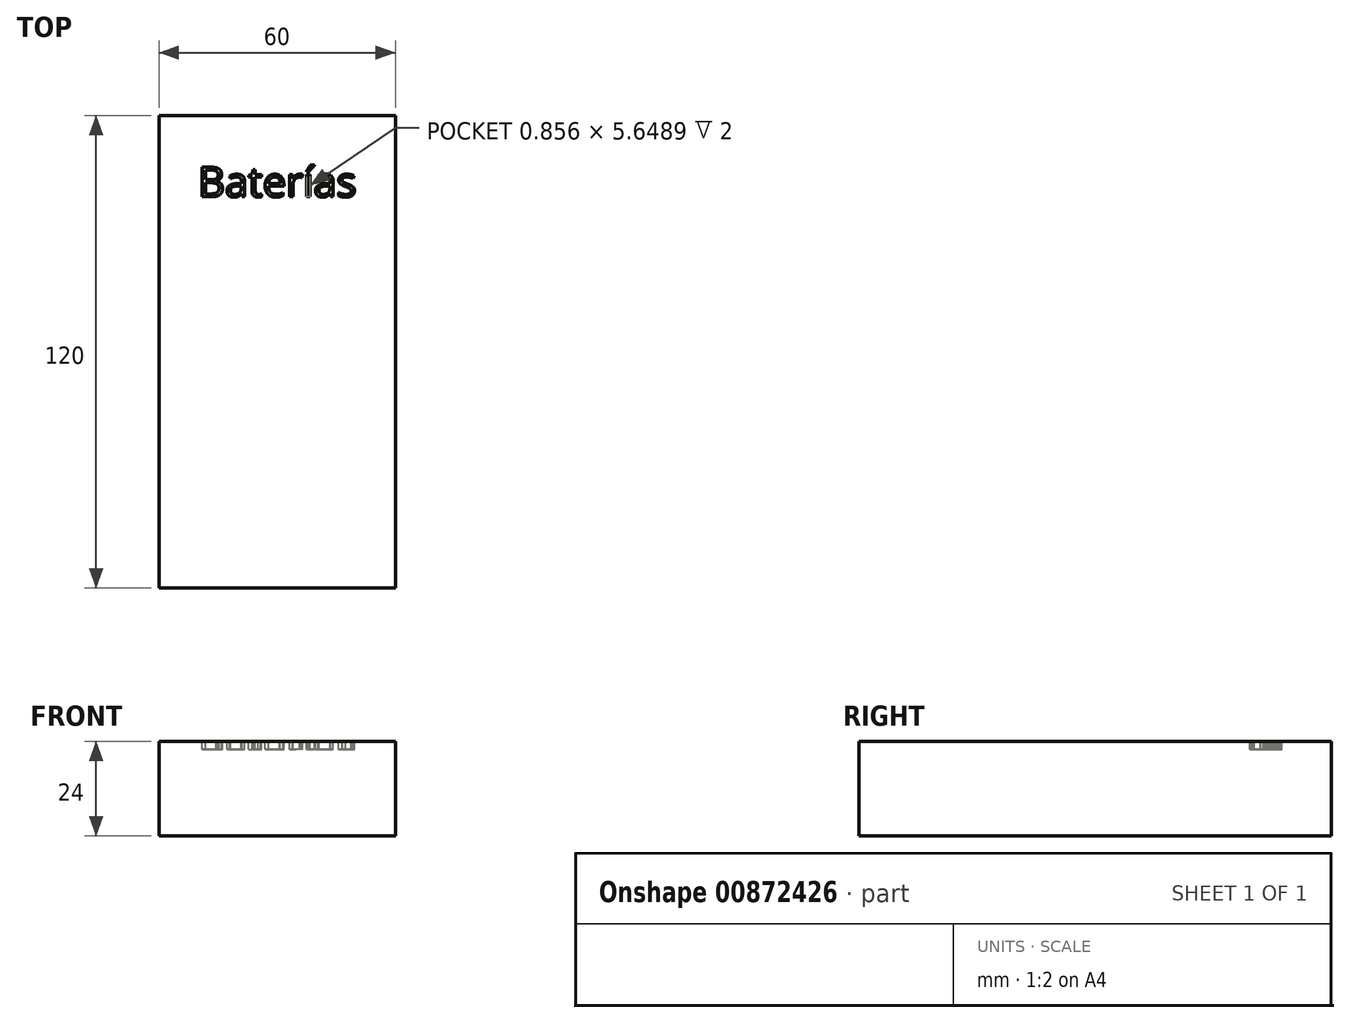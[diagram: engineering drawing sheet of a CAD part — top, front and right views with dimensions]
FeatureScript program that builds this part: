
annotation { "Feature Type Name" : "Feature", "Feature Type Description" : "" }
export const myFeature = defineFeature(function(context is Context, id is Id, definition is map)
    precondition{}
    {
        {
            var Q0;
            Q0=qCreatedBy(makeId("Top.planeOp"),FACE);
            var sketch = newSketch(context, id + "F0", { "sketchPlane" : qUnion([Q0])});
            skLineSegment(sketch, "E0.bottom", {"start": v(30, -60) * mm, "end": v(-30, -60) * mm});
            skLineSegment(sketch, "E0.top", {"start": v(30, 60) * mm, "end": v(-30, 60) * mm});
            skLineSegment(sketch, "E0.left", {"start": v(30, -60) * mm, "end": v(30, 60) * mm});
            skLineSegment(sketch, "E0.right", {"start": v(-30, -60) * mm, "end": v(-30, 60) * mm});
            skPoint(sketch, "E0.middle", {"position": v(0, 0) * mm});
            skSolve(sketch);
        }
        {
            var Q0;
            Q0=makeQuery(id+"F0.imprint","IMPRINT",FACE,{"disambiguationData":[TD([[makeQuery(id+"F0.imprint","IMPRINT",EDGE,{"derivedFrom":sQuery(id+"F0.wireOp",EDGE,"E0.bottom")}),-1.0]])]});
            extrude(context, id + "F1", {"entities" : qUnion([Q0]), "depth" : 24 * mm, "offsetDistance" : 25 * mm});
        }
        {
            var Q0;
            Q0=makeQuery(id+"F1.opExtrude","CAP_FACE",FACE,{"disambiguationData":[OSD([sQuery(id+"F0.wireOp",EDGE,"E0.bottom"),sQuery(id+"F0.wireOp",EDGE,"E0.top"),sQuery(id+"F0.wireOp",EDGE,"E0.left"),sQuery(id+"F0.wireOp",EDGE,"E0.right")])],"isStart":false});
            var sketch = newSketch(context, id + "F2", { "sketchPlane" : qUnion([Q0])});
            skText(sketch, "E1", { "text": "Baterías", "fontName": "OpenSans-Regular.ttf"});
            const initialGuessF2  = {"E1": [-0.02013, 0.03938, 1, 0, 0.0076]};
            skSetInitialGuess(sketch, initialGuessF2);
            skSolve(sketch);
        }
        {
            var Q0;
            Q0=makeQuery(id+"F2.imprint","IMPRINT",FACE,{"disambiguationData":[TD([[makeQuery(id+"F2.imprint","IMPRINT",EDGE,{"derivedFrom":sQuery(id+"F2.wireOp",EDGE,"E1.sketch_text.stroke-0")}),-1.0]])]});
            var Q1;
            Q1=makeQuery(id+"F2.imprint","IMPRINT",FACE,{"disambiguationData":[TD([[makeQuery(id+"F2.imprint","IMPRINT",EDGE,{"derivedFrom":sQuery(id+"F2.wireOp",EDGE,"E1.sketch_text.stroke-25")}),-1.0]])]});
            var Q2;
            Q2=makeQuery(id+"F2.imprint","IMPRINT",FACE,{"disambiguationData":[TD([[makeQuery(id+"F2.imprint","IMPRINT",EDGE,{"derivedFrom":sQuery(id+"F2.wireOp",EDGE,"E1.sketch_text.stroke-52")}),-1.0]])]});
            var Q3;
            Q3=makeQuery(id+"F2.imprint","IMPRINT",FACE,{"disambiguationData":[TD([[makeQuery(id+"F2.imprint","IMPRINT",EDGE,{"derivedFrom":sQuery(id+"F2.wireOp",EDGE,"E1.sketch_text.stroke-71")}),-1.0]])]});
            var Q4;
            Q4=makeQuery(id+"F2.imprint","IMPRINT",FACE,{"disambiguationData":[TD([[makeQuery(id+"F2.imprint","IMPRINT",EDGE,{"derivedFrom":sQuery(id+"F2.wireOp",EDGE,"E1.sketch_text.stroke-90")}),-1.0]])]});
            var Q5;
            Q5=makeQuery(id+"F2.imprint","IMPRINT",FACE,{"disambiguationData":[TD([[makeQuery(id+"F2.imprint","IMPRINT",EDGE,{"derivedFrom":sQuery(id+"F2.wireOp",EDGE,"E1.sketch_text.stroke-107")}),-1.0]])]});
            var Q6;
            Q6=makeQuery(id+"F2.imprint","IMPRINT",FACE,{"disambiguationData":[TD([[makeQuery(id+"F2.imprint","IMPRINT",EDGE,{"derivedFrom":sQuery(id+"F2.wireOp",EDGE,"E1.sketch_text.stroke-103")}),-1.0]])]});
            var Q7;
            Q7=makeQuery(id+"F2.imprint","IMPRINT",FACE,{"disambiguationData":[TD([[makeQuery(id+"F2.imprint","IMPRINT",EDGE,{"derivedFrom":sQuery(id+"F2.wireOp",EDGE,"E1.sketch_text.stroke-115")}),-1.0]])]});
            var Q8;
            Q8=makeQuery(id+"F2.imprint","IMPRINT",FACE,{"disambiguationData":[TD([[makeQuery(id+"F2.imprint","IMPRINT",EDGE,{"derivedFrom":sQuery(id+"F2.wireOp",EDGE,"E1.sketch_text.stroke-142")}),-1.0]])]});
            extrude(context, id + "F3", {"entities" : qUnion([Q0, Q1, Q2, Q3, Q4, Q5, Q6, Q7, Q8]), "operationType" : NewBodyOperationType.REMOVE, "oppositeDirection" : true, "depth" : 2 * mm, "offsetDistance" : 25 * mm});
        }
    });
